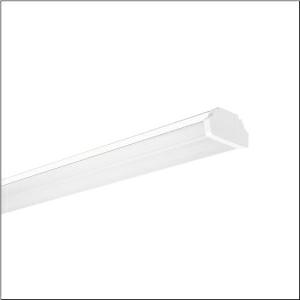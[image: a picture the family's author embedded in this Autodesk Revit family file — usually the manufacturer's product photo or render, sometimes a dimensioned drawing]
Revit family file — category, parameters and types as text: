
# Revit family: dus_r__31_ho_53bd812c1v6105_6b08
name_source: partatom
category: Lighting Fixtures
units: mm (PartAtom-declared; Revit-internal decimal feet)

## family parameters
Cut with Voids When Loaded = No
Host = Face
Light Source = No
Part Type = Normal
Room Calculation Point = No
Round Connector Dimension = Use Diameter
Shared = No

## types (1)
- --- (1 x LED, 10560 lm, 63.8 W, 6500K)
    Apparent Load = 64 VA
    CIE Flux Codes = 47 80 95 92 100
    Color Rendering = 80
    Color Temperature = 6500K
    Default Elevation = 1800 mm
    Description = DUS® 31 HO, luminaire insert, of sheet steel, coil coated, white, length: 1.535mm, width: 81mm, height: 90mm, 5x system unit, system units: 307mm, LED rated luminous flux: 10.560lm, light colour: 865, control gear: ON/OFF Multilumen, CLOi, control gear: ECG Multilumen, with plug, 3-pole, with phase selection, mains connection: 220..240V, AC, 50/60Hz, start of lifetime: 64W, end of service life: 73W, through-wiring accessed according to module size, primary optical cover: cover, of PMMA, light emission: direct distribution, primary light characteristic: symmetric, protection rating (complete): IP20, protection rating (LED compartment): IP50, insulation class (complete): insulation class I (protective earthing), certification: CE, ENEC, VDE, UKCA, impact resistance: IK03, permissible ambient temperature for indoor applications: -35..+35°C, corresponds to IFS (International Featured Standards) requirements for safety and quality in the food industry, reducing of maximum allowable ambient temperature of 5°C with ceiling mounting, packaging unit: 1 piece
    Height = 95 mm
    Lamp = 1 x LED
    Lamp Light Flux = 10560 lm
    Lamp Power = 63.8 W
    Lamp count = 1
    Length = 1535 mm
    Luminous efficacy = 166 lm/W
    Manufacturer = Siteco
    ModVariant = No
    Model = 53BD812C1V6105
    Mounting Place = Ceiling
    Mounting Type = Pendant
    Number of Poles = 1
    OnlyDefault = Yes
    Power Factor = 1
    Product Name = DUS® 31 HO
    Product group = luminaire insert
    ProductGroupID = 901
    Protection Class = Protection class I
    Protection Degree = IP 20
    RLX_Detail_Level = 1
    RLX_Emergency_Light_Flux = 0 lm
    RLX_Emergency_Type = 0
    RLX_Emergency_Type_DB = No
    RlxData = <blob elided: 39893 chars, md5=bd569c9f>
    Socket = socket
    Standby Power = 0 W
    System Light Flux = 10560 lm
    System Power = 64 W
    Type Comments = factory setting: luminous flux: 100 % | (A | C | E) | 144 mA
    Type Image = l_1313537.jpg
    URL = http://relux.com
    VarID = @adj_154907
    Voltage = 0 V
    Weight = 0.00 kg
    Width = 81 mm

## geometry (parser evidence)
native form markers: Blend x4, Sweep x13
no freeform markers — native parametric forms only
